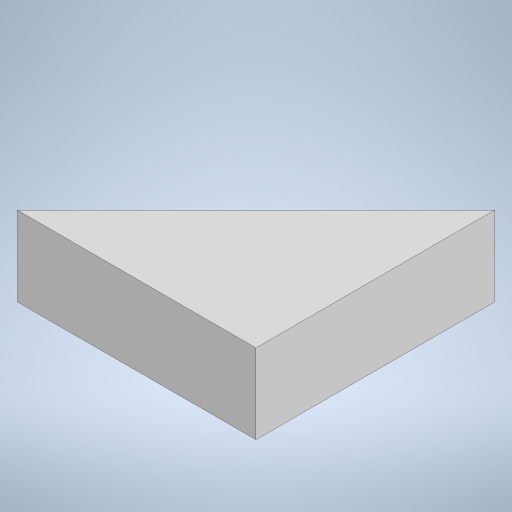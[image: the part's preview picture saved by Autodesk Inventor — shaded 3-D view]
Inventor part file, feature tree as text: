
AUTODESK INVENTOR PART (.ipt)
format: ipt  version: 2023 (Build 270158000, 158)  size: 195,584 bytes
history: native  units: mm
features: extrude x1, sketch x1
ambient origin geometry x8: Origin, YZ Plane, XZ Plane, XY Plane, X Axis, Y Axis, Z Axis, Center Point
bodies: Solid1 (feature_tree)
feature tree (2):
  extrude  "Extrusion1"  Depth=5.0mm TaperAngle=0.0deg
  sketch  "Sketch1"  dims[d0=15.0mm d1=5.0mm d2=0.0mm]
